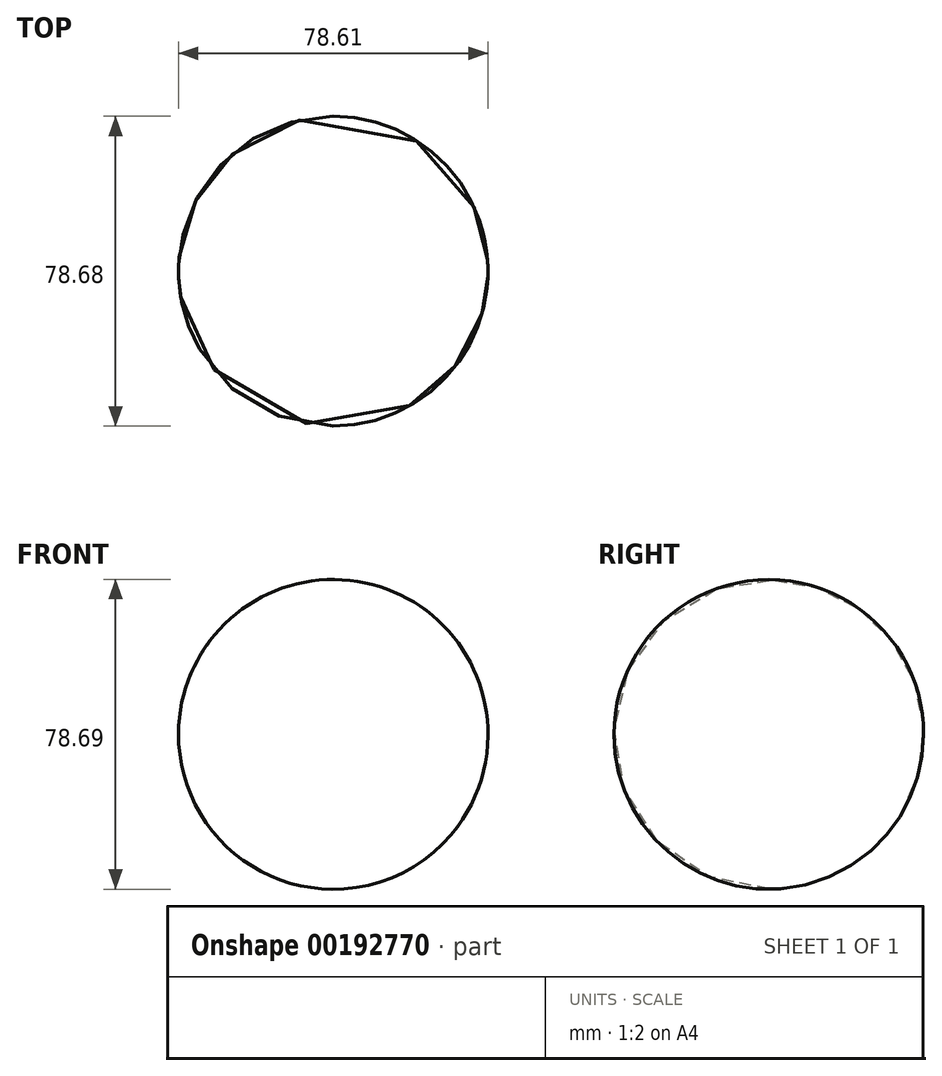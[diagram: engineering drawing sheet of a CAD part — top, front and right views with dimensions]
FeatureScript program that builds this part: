
annotation { "Feature Type Name" : "Feature", "Feature Type Description" : "" }
export const myFeature = defineFeature(function(context is Context, id is Id, definition is map)
    precondition{}
    {
        {
            var Q0;
            Q0=qCreatedBy(makeId("Front.planeOp"),FACE);
            var sketch = newSketch(context, id + "F0", { "sketchPlane" : qUnion([Q0])});
            skArc(sketch, "E0", {"start": v(39.3, -0.28) * mm, "mid": v(0.32, 39.3) * mm, "end": v(-39.3, 0.36) * mm});
            skLineSegment(sketch, "E1", {"start": v(-39.3, 0.36) * mm, "end": v(39.3, -0.28) * mm});
            skSolve(sketch);
        }
        {
            var Q0;
            Q0=makeQuery(id+"F0.imprint","IMPRINT",FACE,{"disambiguationData":[TD([[makeQuery(id+"F0.imprint","IMPRINT",EDGE,{"derivedFrom":sQuery(id+"F0.wireOp",EDGE,"E0")}),1.0]])]});
            var Q1;
            Q1=sQuery(id+"F0.wireOp",EDGE,"E1");
            revolve(context, id + "F1", {"entities" : qUnion([Q0]), "axis" : qUnion([Q1]), "revolveType" : RevolveType.FULL});
        }
    });
